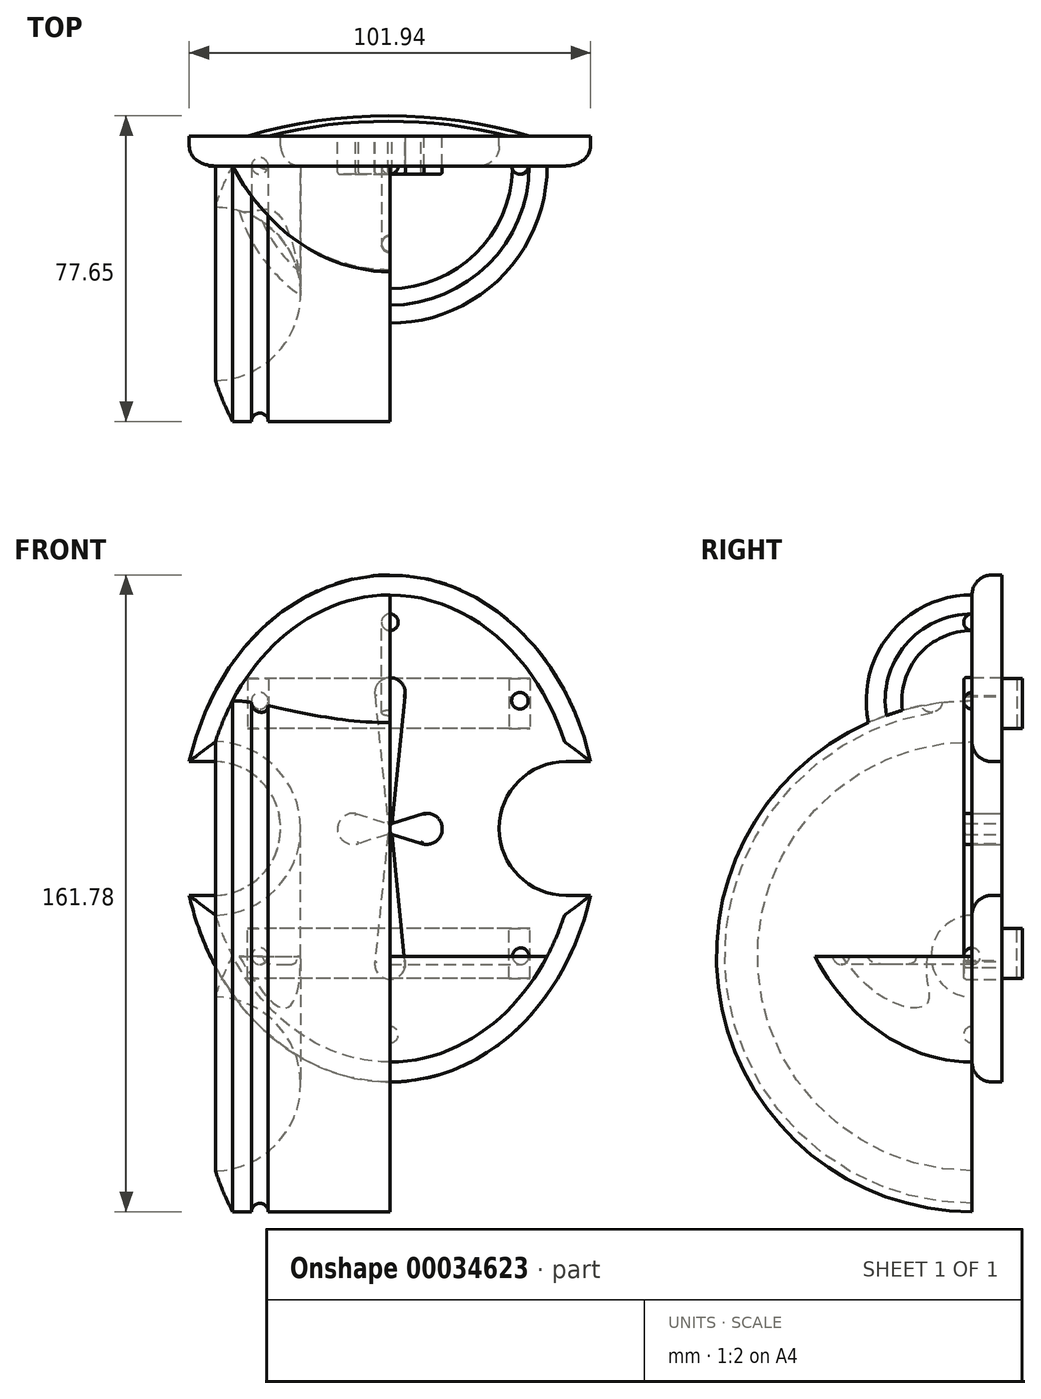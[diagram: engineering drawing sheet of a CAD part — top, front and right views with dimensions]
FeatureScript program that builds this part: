
annotation { "Feature Type Name" : "Feature", "Feature Type Description" : "" }
export const myFeature = defineFeature(function(context is Context, id is Id, definition is map)
    precondition{}
    {
        {
            var Q0;
            Q0=qCreatedBy(makeId("Front.planeOp"),FACE);
            var sketch = newSketch(context, id + "F0", { "sketchPlane" : qUnion([Q0])});
            skEllipticalArc(sketch, "E0", {});
            skLineSegment(sketch, "E1", {"start": v(-52.84, 0) * mm, "end": v(52.84, 0) * mm, "construction": true});
            skLineSegment(sketch, "E2", {"start": v(0, 64.42) * mm, "end": v(0, -64.42) * mm, "construction": true});
            skLineSegment(sketch, "E3.rect.bottom", {"start": v(-50.97, 16.98) * mm, "end": v(-44.74, 16.98) * mm});
            skLineSegment(sketch, "E3.rect.top", {"start": v(-50.97, -16.98) * mm, "end": v(-44.74, -16.98) * mm});
            skPoint(sketch, "E3.rect.middle", {"position": v(-52.84, 0) * mm});
            skArc(sketch, "E4", {"start": v(-44.74, -16.98) * mm, "mid": v(-27.76, 0) * mm, "end": v(-44.74, 16.98) * mm});
            skPoint(sketch, "E5.orphan", {"position": v(-60.94, -16.98) * mm});
            skPoint(sketch, "E6.orphan", {"position": v(-60.94, 16.98) * mm});
            skArc(sketch, "E7.MirrorCS", {"start": v(44.74, -16.98) * mm, "mid": v(27.76, 0) * mm, "end": v(44.74, 16.98) * mm});
            skLineSegment(sketch, "E8.MirrorCS", {"start": v(50.97, 16.98) * mm, "end": v(44.74, 16.98) * mm});
            skLineSegment(sketch, "E9.MirrorCS", {"start": v(50.97, -16.98) * mm, "end": v(44.74, -16.98) * mm});
            skEllipticalArc(sketch, "E10.trimOffspring", {});
            const initialGuessF0  = {"E0": [0, 0, 0, 1, 0.06441504676594614, 0.05284112137579867, 1.837603001446633, 4.4455823057329535], "E10.trimOffspring": [0, 0, 0, 1, 0.06441504676594614, 0.05284112137579867, 4.979195655036426, 1.30398965214316]};
            skSetInitialGuess(sketch, initialGuessF0);
            skSolve(sketch);
        }
        {
            var Q0;
            Q0 = qSketchRegion(id + "F0", true);
            extrude(context, id + "F1", {"entities" : qUnion([Q0]), "depth" : 7.62 * mm});
        }
        {
            var Q0;
            Q0=makeQuery(id+"F1.opExtrude","CAP_EDGE",EDGE,{"disambiguationData":[OSD([sQuery(id+"F0.wireOp",EDGE,"E10.trimOffspring")])],"isStart":false});
            var Q1;
            Q1=makeQuery(id+"F1.opExtrude","CAP_EDGE",EDGE,{"disambiguationData":[OSD([sQuery(id+"F0.wireOp",EDGE,"E7.MirrorCS")])],"isStart":false});
            var Q2;
            Q2=makeQuery(id+"F1.opExtrude","CAP_EDGE",EDGE,{"disambiguationData":[OSD([sQuery(id+"F0.wireOp",EDGE,"E0")])],"isStart":false});
            var Q3;
            Q3=makeQuery(id+"F1.opExtrude","CAP_EDGE",EDGE,{"disambiguationData":[OSD([sQuery(id+"F0.wireOp",EDGE,"E9.MirrorCS")])],"isStart":false});
            var Q4;
            Q4=makeQuery(id+"F1.opExtrude","CAP_EDGE",EDGE,{"disambiguationData":[OSD([sQuery(id+"F0.wireOp",EDGE,"E4")])],"isStart":false});
            var Q5;
            Q5=makeQuery(id+"F1.opExtrude","CAP_EDGE",EDGE,{"disambiguationData":[OSD([sQuery(id+"F0.wireOp",EDGE,"E3.rect.top")])],"isStart":false});
            var Q6;
            Q6=makeQuery(id+"F1.opExtrude","CAP_EDGE",EDGE,{"disambiguationData":[OSD([sQuery(id+"F0.wireOp",EDGE,"E3.rect.bottom")])],"isStart":false});
            var Q7;
            Q7=makeQuery(id+"F1.opExtrude","CAP_EDGE",EDGE,{"disambiguationData":[OSD([sQuery(id+"F0.wireOp",EDGE,"E8.MirrorCS")])],"isStart":false});
            fillet(context, id + "F2", {"entities" : qUnion([Q0, Q1, Q2, Q3, Q4, Q5, Q6, Q7]), "radius" : 5.08 * mm, "tangentPropagation" : true, "allowEdgeOverflow" : false});
        }
        {
            var Q0;
            Q0=qCreatedBy(makeId("Top.planeOp"),FACE);
            cPlane(context, id + "F3", {"entities" : qUnion([Q0]), "cplaneType" : CPlaneType.OFFSET, "offset" : 31.75 * mm, "width" : 152.4 * mm, "height" : 152.4 * mm});
        }
        {
            var Q0;
            Q0=qCreatedBy(id+"F3.planeOp",FACE);
            var sketch = newSketch(context, id + "F4", { "sketchPlane" : qUnion([Q0])});
            skArc(sketch, "E11", {"start": v(35.55, 0) * mm, "mid": v(-0.33, 5.12) * mm, "end": v(-36.21, 0) * mm});
            skArc(sketch, "E12.0", {"start": v(30.21, 0) * mm, "mid": v(-0.33, 3.74) * mm, "end": v(-30.88, 0) * mm});
            skLineSegment(sketch, "E13", {"start": v(-36.21, 0) * mm, "end": v(35.55, 0) * mm});
            skSolve(sketch);
        }
        {
            var Q0;
            {var subQ2=sQuery(id+"F4.wireOp",EDGE,"E11");Q0=makeQuery(id+"F4.imprint","IMPRINT",FACE,{"disambiguationData":[TD([[makeQuery(id+"F4.imprint","IMPRINT",EDGE,{"derivedFrom":subQ2}),1.0]])]});}
            extrude(context, id + "F5", {"entities" : qUnion([Q0]), "endBound" : BoundingType.SYMMETRIC, "depth" : 12.7 * mm});
        }
        {
            var Q0;
            Q0=makeQuery(id+"F5.opExtrude","SWEPT_BODY",BODY,{"disambiguationData":[OSD([sQuery(id+"F4.wireOp",EDGE,"E11"),sQuery(id+"F4.wireOp",EDGE,"E12.0"),sQuery(id+"F4.wireOp",EDGE,"E13")])]});
            var Q1;
            Q1=qCreatedBy(makeId("Top.planeOp"),FACE);
            mirror(context, id + "F6", {"operationType" : NewBodyOperationType.ADD, "entities" : qUnion([Q0]), "mirrorPlane" : qUnion([Q1])});
        }
        {
            var Q0;
            Q0=makeQuery(id+"F1.opExtrude","CAP_FACE",FACE,{"disambiguationData":[OSD([sQuery(id+"F0.wireOp",EDGE,"E0"),sQuery(id+"F0.wireOp",EDGE,"E3.rect.bottom"),sQuery(id+"F0.wireOp",EDGE,"E3.rect.top"),sQuery(id+"F0.wireOp",EDGE,"E4"),sQuery(id+"F0.wireOp",EDGE,"E7.MirrorCS"),sQuery(id+"F0.wireOp",EDGE,"E8.MirrorCS"),sQuery(id+"F0.wireOp",EDGE,"E9.MirrorCS"),sQuery(id+"F0.wireOp",EDGE,"E10.trimOffspring")])],"isStart":false});
            var sketch = newSketch(context, id + "F7", { "sketchPlane" : qUnion([Q0])});
            skArc(sketch, "E14.0", {"start": v(-44.33, 22.06) * mm, "mid": v(-22.68, 0) * mm, "end": v(-44.33, -22.06) * mm});
            skArc(sketch, "E15.1", {"start": v(44.33, -22.06) * mm, "mid": v(22.68, 0) * mm, "end": v(44.33, 22.06) * mm});
            skFitSpline(sketch, "E16.2", {"points": [v(45.82, 17) * mm, v(44.63, 21.22) * mm, v(43.48, 24.58) * mm, v(42.51, 27.05) * mm, v(41.46, 29.46) * mm, v(40.3, 31.83) * mm, v(39.05, 34.15) * mm, v(37.7, 36.41) * mm, v(36.26, 38.62) * mm, v(34.7, 40.77) * mm, v(33.04, 42.84) * mm, v(31.3, 44.81) * mm, v(29.46, 46.7) * mm, v(27.52, 48.5) * mm, v(25.82, 49.9) * mm, v(24.41, 50.98) * mm, v(22.98, 52) * mm, v(21.14, 53.22) * mm, v(18.85, 54.53) * mm, v(16.5, 55.7) * mm, v(14.46, 56.56) * mm, v(12.8, 57.17) * mm, v(11.11, 57.72) * mm, v(9, 58.3) * mm, v(6.42, 58.82) * mm, v(3.81, 59.17) * mm, v(1.18, 59.35) * mm, v(-1.5, 59.34) * mm, v(-4.15, 59.14) * mm, v(-6.77, 58.76) * mm, v(-9.33, 58.22) * mm, v(-11.84, 57.5) * mm, v(-14.31, 56.63) * mm, v(-16.73, 55.59) * mm, v(-19.11, 54.39) * mm, v(-21.4, 53.06) * mm, v(-23.58, 51.6) * mm, v(-25.68, 50.03) * mm, v(-27.7, 48.34) * mm, v(-29.63, 46.53) * mm, v(-31.48, 44.62) * mm, v(-33.2, 42.63) * mm, v(-34.84, 40.58) * mm, v(-36.37, 38.45) * mm, v(-37.8, 36.25) * mm, v(-39.14, 34) * mm, v(-40.39, 31.67) * mm, v(-41.54, 29.28) * mm, v(-42.6, 26.85) * mm, v(-43.87, 23.56) * mm, v(-45.21, 19.34) * mm, v(-46.43, 14.21) * mm, v(-47.13, 9.87) * mm, v(-47.5, 6.36) * mm, v(-47.74, 2.84) * mm, v(-47.8, -1.54) * mm, v(-47.56, -5.9) * mm, v(-47.17, -9.38) * mm, v(-46.79, -11.99) * mm, v(-46.3, -14.58) * mm, v(-45.53, -18.04) * mm, v(-44.33, -22.26) * mm, v(-42.51, -27.19) * mm, v(-40.67, -31.17) * mm, v(-38.98, -34.29) * mm, v(-37.62, -36.55) * mm, v(-36.16, -38.75) * mm, v(-34.1, -41.58) * mm, v(-31.83, -44.27) * mm, v(-29.35, -46.8) * mm, v(-26.75, -49.2) * mm, v(-23.99, -51.35) * mm, v(-21.41, -53.03) * mm, v(-19.9, -53.93) * mm, v(-18.34, -54.79) * mm, v(-16.36, -55.76) * mm, v(-13.93, -56.78) * mm, v(-11.44, -57.63) * mm, v(-9.32, -58.2) * mm, v(-7.6, -58.58) * mm, v(-5.84, -58.9) * mm, v(-3.66, -59.19) * mm, v(-1.04, -59.35) * mm, v(1.58, -59.33) * mm, v(4.2, -59.13) * mm, v(6.38, -58.82) * mm, v(8.12, -58.47) * mm, v(9.84, -58.07) * mm, v(11.95, -57.47) * mm, v(14.42, -56.58) * mm, v(16.83, -55.54) * mm, v(19.19, -54.35) * mm, v(21.48, -53) * mm, v(23.7, -51.52) * mm, v(25.8, -49.93) * mm, v(27.8, -48.24) * mm, v(29.72, -46.44) * mm, v(31.54, -44.55) * mm, v(32.98, -42.9) * mm, v(34.1, -41.52) * mm, v(35.17, -40.12) * mm, v(36.45, -38.33) * mm, v(37.88, -36.13) * mm, v(39.65, -33.13) * mm, v(41.6, -29.26) * mm, v(43.25, -25.24) * mm, v(44.39, -21.93) * mm, v(45.02, -19.82) * mm, v(45.48, -18.12) * mm, v(45.9, -16.41) * mm, v(46.37, -14.27) * mm, v(46.84, -11.7) * mm, v(47.33, -8.25) * mm, v(47.72, -3.9) * mm, v(47.8, 0.46) * mm, v(47.67, 3.98) * mm, v(47.41, 7.5) * mm, v(46.86, 11.84) * mm, v(45.82, 17) * mm, v(44.63, 21.22) * mm, v(43.48, 24.58) * mm]});
            skFitSpline(sketch, "E17.2", {"points": [v(45.82, 17) * mm, v(44.63, 21.22) * mm, v(43.48, 24.58) * mm, v(42.51, 27.05) * mm, v(41.46, 29.46) * mm, v(40.3, 31.83) * mm, v(39.05, 34.15) * mm, v(37.7, 36.41) * mm, v(36.26, 38.62) * mm, v(34.7, 40.77) * mm, v(33.04, 42.84) * mm, v(31.3, 44.81) * mm, v(29.46, 46.7) * mm, v(27.52, 48.5) * mm, v(25.82, 49.9) * mm, v(24.41, 50.98) * mm, v(22.98, 52) * mm, v(21.14, 53.22) * mm, v(18.85, 54.53) * mm, v(16.5, 55.7) * mm, v(14.46, 56.56) * mm, v(12.8, 57.17) * mm, v(11.11, 57.72) * mm, v(9, 58.3) * mm, v(6.42, 58.82) * mm, v(3.81, 59.17) * mm, v(1.18, 59.35) * mm, v(-1.5, 59.34) * mm, v(-4.15, 59.14) * mm, v(-6.77, 58.76) * mm, v(-9.33, 58.22) * mm, v(-11.84, 57.5) * mm, v(-14.31, 56.63) * mm, v(-16.73, 55.59) * mm, v(-19.11, 54.39) * mm, v(-21.4, 53.06) * mm, v(-23.58, 51.6) * mm, v(-25.68, 50.03) * mm, v(-27.7, 48.34) * mm, v(-29.63, 46.53) * mm, v(-31.48, 44.62) * mm, v(-33.2, 42.63) * mm, v(-34.84, 40.58) * mm, v(-36.37, 38.45) * mm, v(-37.8, 36.25) * mm, v(-39.14, 34) * mm, v(-40.39, 31.67) * mm, v(-41.54, 29.28) * mm, v(-42.6, 26.85) * mm, v(-43.87, 23.56) * mm, v(-45.21, 19.34) * mm, v(-46.43, 14.21) * mm, v(-47.13, 9.87) * mm, v(-47.5, 6.36) * mm, v(-47.74, 2.84) * mm, v(-47.8, -1.54) * mm, v(-47.56, -5.9) * mm, v(-47.17, -9.38) * mm, v(-46.79, -11.99) * mm, v(-46.3, -14.58) * mm, v(-45.53, -18.04) * mm, v(-44.33, -22.26) * mm, v(-42.51, -27.19) * mm, v(-40.67, -31.17) * mm, v(-38.98, -34.29) * mm, v(-37.62, -36.55) * mm, v(-36.16, -38.75) * mm, v(-34.1, -41.58) * mm, v(-31.83, -44.27) * mm, v(-29.35, -46.8) * mm, v(-26.75, -49.2) * mm, v(-23.99, -51.35) * mm, v(-21.41, -53.03) * mm, v(-19.9, -53.93) * mm, v(-18.34, -54.79) * mm, v(-16.36, -55.76) * mm, v(-13.93, -56.78) * mm, v(-11.44, -57.63) * mm, v(-9.32, -58.2) * mm, v(-7.6, -58.58) * mm, v(-5.84, -58.9) * mm, v(-3.66, -59.19) * mm, v(-1.04, -59.35) * mm, v(1.58, -59.33) * mm, v(4.2, -59.13) * mm, v(6.38, -58.82) * mm, v(8.12, -58.47) * mm, v(9.84, -58.07) * mm, v(11.95, -57.47) * mm, v(14.42, -56.58) * mm, v(16.83, -55.54) * mm, v(19.19, -54.35) * mm, v(21.48, -53) * mm, v(23.7, -51.52) * mm, v(25.8, -49.93) * mm, v(27.8, -48.24) * mm, v(29.72, -46.44) * mm, v(31.54, -44.55) * mm, v(32.98, -42.9) * mm, v(34.1, -41.52) * mm, v(35.17, -40.12) * mm, v(36.45, -38.33) * mm, v(37.88, -36.13) * mm, v(39.65, -33.13) * mm, v(41.6, -29.26) * mm, v(43.25, -25.24) * mm, v(44.39, -21.93) * mm, v(45.02, -19.82) * mm, v(45.48, -18.12) * mm, v(45.9, -16.41) * mm, v(46.37, -14.27) * mm, v(46.84, -11.7) * mm, v(47.33, -8.25) * mm, v(47.72, -3.9) * mm, v(47.8, 0.46) * mm, v(47.67, 3.98) * mm, v(47.41, 7.5) * mm, v(46.86, 11.84) * mm, v(45.82, 17) * mm, v(44.63, 21.22) * mm, v(43.48, 24.58) * mm]});
            skFitSpline(sketch, "E17.3", {"points": [v(-45.82, -17) * mm, v(-44.63, -21.23) * mm, v(-43.47, -24.58) * mm, v(-42.51, -27.05) * mm, v(-41.45, -29.47) * mm, v(-40.3, -31.84) * mm, v(-39.05, -34.15) * mm, v(-37.7, -36.41) * mm, v(-36.25, -38.62) * mm, v(-34.7, -40.77) * mm, v(-33.04, -42.84) * mm, v(-31.3, -44.82) * mm, v(-29.45, -46.7) * mm, v(-27.52, -48.5) * mm, v(-25.82, -49.9) * mm, v(-24.4, -50.98) * mm, v(-22.97, -52.01) * mm, v(-21.13, -53.22) * mm, v(-18.85, -54.53) * mm, v(-16.5, -55.7) * mm, v(-14.46, -56.56) * mm, v(-12.79, -57.17) * mm, v(-11.1, -57.72) * mm, v(-8.99, -58.3) * mm, v(-6.41, -58.83) * mm, v(-3.8, -59.18) * mm, v(-1.17, -59.35) * mm, v(1.5, -59.34) * mm, v(4.16, -59.14) * mm, v(6.77, -58.76) * mm, v(9.33, -58.22) * mm, v(11.85, -57.5) * mm, v(14.32, -56.63) * mm, v(16.74, -55.59) * mm, v(19.12, -54.39) * mm, v(21.4, -53.05) * mm, v(23.59, -51.6) * mm, v(25.68, -50.02) * mm, v(27.7, -48.33) * mm, v(29.63, -46.53) * mm, v(31.48, -44.62) * mm, v(33.21, -42.63) * mm, v(34.84, -40.57) * mm, v(36.37, -38.45) * mm, v(37.8, -36.25) * mm, v(39.14, -34) * mm, v(40.39, -31.67) * mm, v(41.54, -29.28) * mm, v(42.6, -26.85) * mm, v(43.87, -23.55) * mm, v(45.21, -19.34) * mm, v(46.43, -14.2) * mm, v(47.13, -9.87) * mm, v(47.5, -6.35) * mm, v(47.74, -2.83) * mm, v(47.8, 1.55) * mm, v(47.56, 5.9) * mm, v(47.17, 9.39) * mm, v(46.79, 11.99) * mm, v(46.3, 14.59) * mm, v(45.53, 18.04) * mm, v(44.33, 22.26) * mm, v(42.5, 27.2) * mm, v(40.66, 31.17) * mm, v(38.98, 34.29) * mm, v(37.61, 36.56) * mm, v(36.16, 38.75) * mm, v(34.1, 41.59) * mm, v(31.83, 44.27) * mm, v(29.35, 46.8) * mm, v(26.75, 49.2) * mm, v(23.99, 51.35) * mm, v(21.4, 53.04) * mm, v(19.89, 53.93) * mm, v(18.33, 54.79) * mm, v(16.35, 55.76) * mm, v(13.92, 56.78) * mm, v(11.43, 57.63) * mm, v(9.31, 58.2) * mm, v(7.59, 58.59) * mm, v(5.84, 58.9) * mm, v(3.66, 59.2) * mm, v(1.04, 59.35) * mm, v(-1.58, 59.33) * mm, v(-4.2, 59.13) * mm, v(-6.38, 58.82) * mm, v(-8.13, 58.47) * mm, v(-9.85, 58.07) * mm, v(-11.96, 57.47) * mm, v(-14.43, 56.58) * mm, v(-16.84, 55.54) * mm, v(-19.19, 54.35) * mm, v(-21.49, 53) * mm, v(-23.7, 51.52) * mm, v(-25.8, 49.93) * mm, v(-27.81, 48.23) * mm, v(-29.72, 46.44) * mm, v(-31.54, 44.55) * mm, v(-32.99, 42.89) * mm, v(-34.1, 41.52) * mm, v(-35.18, 40.11) * mm, v(-36.45, 38.33) * mm, v(-37.88, 36.13) * mm, v(-39.65, 33.13) * mm, v(-41.6, 29.26) * mm, v(-43.25, 25.24) * mm, v(-44.39, 21.93) * mm, v(-45.02, 19.82) * mm, v(-45.48, 18.12) * mm, v(-45.9, 16.4) * mm, v(-46.37, 14.27) * mm, v(-46.84, 11.7) * mm, v(-47.33, 8.24) * mm, v(-47.72, 3.9) * mm, v(-47.8, -0.46) * mm, v(-47.67, -3.98) * mm, v(-47.41, -7.5) * mm, v(-46.86, -11.85) * mm, v(-45.82, -17) * mm, v(-44.63, -21.23) * mm, v(-43.47, -24.58) * mm]});
            skLineSegment(sketch, "E18", {"start": v(-39.96, 32.45) * mm, "end": v(39.96, 32.45) * mm});
            skLineSegment(sketch, "E19.MirrorCS", {"start": v(-39.96, -32.45) * mm, "end": v(40.19, -32.45) * mm});
            skCircle(sketch, "E20", {"center": v(-33.04, 32.45) * mm, "radius": 2.11 * mm});
            skCircle(sketch, "E21", {"center": v(33.03, 32.45) * mm, "radius": 2.11 * mm});
            skCircle(sketch, "E22", {"center": v(-33.03, -32.45) * mm, "radius": 2.11 * mm});
            skCircle(sketch, "E23", {"center": v(33.25, -32.45) * mm, "radius": 2.11 * mm});
            skLineSegment(sketch, "E24", {"start": v(0, 59.34) * mm, "end": v(0, -59.34) * mm});
            skCircle(sketch, "E25", {"center": v(0, 52.4) * mm, "radius": 2.11 * mm});
            skCircle(sketch, "E26", {"center": v(0, -52.4) * mm, "radius": 2.11 * mm});
            skSolve(sketch);
        }
        {
            var Q0;
            {var subQ0=sQuery(id+"F7.wireOp",EDGE,"E20");var subQ1=sQuery(id+"F7.wireOp",EDGE,"E18");var subQ3=makeQuery(id+"F7.imprint","INTERSECT",VERTEX,{"disambiguationData":[OD(0.0)],"derivedFrom":[subQ1,subQ0]});Q0=makeQuery(id+"F7.imprint","IMPRINT",FACE,{"disambiguationData":[TD([[makeQuery(id+"F7.imprint","IMPRINT",EDGE,{"disambiguationData":[TD([[subQ3,-1.0]])],"derivedFrom":subQ1}),1.0]])]});}
            var Q1;
            Q1=sQuery(id+"F7.wireOp",EDGE,"E18");
            revolve(context, id + "F8", {"operationType" : NewBodyOperationType.ADD, "entities" : qUnion([Q0]), "axis" : qUnion([Q1]), "revolveType" : RevolveType.ONE_DIRECTION, "angle" : 180 * degree});
        }
        {
            var Q0;
            {var subQ0=sQuery(id+"F7.wireOp",EDGE,"E25");var subQ1=sQuery(id+"F7.wireOp",EDGE,"E24");var subQ3=makeQuery(id+"F7.imprint","INTERSECT",VERTEX,{"disambiguationData":[OD(0.0)],"derivedFrom":[subQ1,subQ0]});Q0=makeQuery(id+"F7.imprint","IMPRINT",FACE,{"disambiguationData":[TD([[makeQuery(id+"F7.imprint","IMPRINT",EDGE,{"disambiguationData":[TD([[subQ3,1.0]])],"derivedFrom":subQ1}),1.0]])]});}
            var Q1;
            Q1=sQuery(id+"F7.wireOp",EDGE,"E24");
            revolve(context, id + "F9", {"operationType" : NewBodyOperationType.ADD, "entities" : qUnion([Q0]), "axis" : qUnion([Q1]), "revolveType" : RevolveType.ONE_DIRECTION, "angle" : 180 * degree});
        }
        {
            var Q0;
            {var subQ0=sQuery(id+"F7.wireOp",EDGE,"E21");var subQ1=sQuery(id+"F7.wireOp",EDGE,"E18");var subQ3=makeQuery(id+"F7.imprint","INTERSECT",VERTEX,{"disambiguationData":[OD(0.0)],"derivedFrom":[subQ1,subQ0]});Q0=makeQuery(id+"F7.imprint","IMPRINT",FACE,{"disambiguationData":[TD([[makeQuery(id+"F7.imprint","IMPRINT",EDGE,{"disambiguationData":[TD([[subQ3,-1.0]])],"derivedFrom":subQ1}),-1.0]])]});}
            var Q1;
            Q1=sQuery(id+"F7.wireOp",EDGE,"E18");
            revolve(context, id + "F10", {"operationType" : NewBodyOperationType.ADD, "entities" : qUnion([Q0]), "axis" : qUnion([Q1]), "revolveType" : RevolveType.ONE_DIRECTION, "oppositeDirection" : true, "angle" : 180 * degree});
        }
        {
            var Q0;
            {var subQ0=sQuery(id+"F7.wireOp",EDGE,"E22");var subQ1=sQuery(id+"F7.wireOp",EDGE,"E19.MirrorCS");var subQ3=makeQuery(id+"F7.imprint","INTERSECT",VERTEX,{"disambiguationData":[OD(0.0)],"derivedFrom":[subQ1,subQ0]});Q0=makeQuery(id+"F7.imprint","IMPRINT",FACE,{"disambiguationData":[TD([[makeQuery(id+"F7.imprint","IMPRINT",EDGE,{"disambiguationData":[TD([[subQ3,-1.0]])],"derivedFrom":subQ1}),1.0]])]});}
            var Q1;
            Q1=sQuery(id+"F7.wireOp",EDGE,"E19.MirrorCS");
            revolve(context, id + "F11", {"operationType" : NewBodyOperationType.ADD, "entities" : qUnion([Q0]), "axis" : qUnion([Q1]), "revolveType" : RevolveType.ONE_DIRECTION, "angle" : 180 * degree});
        }
        {
            var Q0;
            {var subQ0=sQuery(id+"F7.wireOp",EDGE,"E23");var subQ1=sQuery(id+"F7.wireOp",EDGE,"E19.MirrorCS");var subQ3=makeQuery(id+"F7.imprint","INTERSECT",VERTEX,{"disambiguationData":[OD(0.0)],"derivedFrom":[subQ1,subQ0]});Q0=makeQuery(id+"F7.imprint","IMPRINT",FACE,{"disambiguationData":[TD([[makeQuery(id+"F7.imprint","IMPRINT",EDGE,{"disambiguationData":[TD([[subQ3,-1.0]])],"derivedFrom":subQ1}),-1.0]])]});}
            var Q1;
            Q1=sQuery(id+"F7.wireOp",EDGE,"E19.MirrorCS");
            revolve(context, id + "F12", {"operationType" : NewBodyOperationType.ADD, "entities" : qUnion([Q0]), "axis" : qUnion([Q1]), "revolveType" : RevolveType.ONE_DIRECTION, "oppositeDirection" : true, "angle" : 180 * degree});
        }
        {
            var Q0;
            {var subQ0=sQuery(id+"F7.wireOp",EDGE,"E26");var subQ1=sQuery(id+"F7.wireOp",EDGE,"E24");var subQ3=makeQuery(id+"F7.imprint","INTERSECT",VERTEX,{"disambiguationData":[OD(0.0)],"derivedFrom":[subQ1,subQ0]});Q0=makeQuery(id+"F7.imprint","IMPRINT",FACE,{"disambiguationData":[TD([[makeQuery(id+"F7.imprint","IMPRINT",EDGE,{"disambiguationData":[TD([[subQ3,1.0]])],"derivedFrom":subQ1}),1.0]])]});}
            var Q1;
            Q1=sQuery(id+"F7.wireOp",EDGE,"E24");
            revolve(context, id + "F13", {"operationType" : NewBodyOperationType.ADD, "entities" : qUnion([Q0]), "axis" : qUnion([Q1]), "revolveType" : RevolveType.ONE_DIRECTION, "angle" : 180 * degree});
        }
        {
            var Q0;
            Q0=qCreatedBy(makeId("Front.planeOp"),FACE);
            var sketch = newSketch(context, id + "F14", { "sketchPlane" : qUnion([Q0])});
            skLineSegment(sketch, "E27.rect.bottom", {"start": v(-1.24, 38.1) * mm, "end": v(3.81, 38.1) * mm});
            skLineSegment(sketch, "E27.rect.top", {"start": v(-1.24, -38.1) * mm, "end": v(1.29, -38.1) * mm});
            skLineSegment(sketch, "E27.rect.left", {"start": v(-3.8, 35.04) * mm, "end": v(-3.8, 33.82) * mm});
            skLineSegment(sketch, "E27.rect.right", {"start": v(3.81, 35.28) * mm, "end": v(3.81, 33.58) * mm});
            skPoint(sketch, "E27.rect.middle", {"position": v(0, 0) * mm});
            skLineSegment(sketch, "E28.rect.bottom", {"start": v(-9.98, 3.81) * mm, "end": v(-8.7, 3.81) * mm});
            skLineSegment(sketch, "E28.rect.top", {"start": v(-10.73, -3.81) * mm, "end": v(-7.95, -3.81) * mm});
            skLineSegment(sketch, "E28.rect.left", {"start": v(-13.22, 0.7) * mm, "end": v(-13.22, -0.9) * mm});
            skLineSegment(sketch, "E28.rect.right", {"start": v(13.22, 0.7) * mm, "end": v(13.22, -0.9) * mm});
            skPoint(sketch, "E29.visualSharp", {"position": v(-3.8, 38.1) * mm});
            skArc(sketch, "E29.filletArc", {"start": v(-3.5, 38.1) * mm, "mid": v(-3.72, 38) * mm, "end": v(-3.8, 37.78) * mm});
            skArc(sketch, "E30", {"start": v(3.81, 33.58) * mm, "mid": v(0.14, 38.3) * mm, "end": v(-3.8, 33.82) * mm});
            skArc(sketch, "E31.MirrorCS", {"start": v(3.8, -33.58) * mm, "mid": v(0.14, -38.3) * mm, "end": v(-3.81, -33.82) * mm});
            skArc(sketch, "E32", {"start": v(-8.7, 3.81) * mm, "mid": v(-13.28, -0.49) * mm, "end": v(-7.95, -3.81) * mm});
            skArc(sketch, "E33.MirrorCS", {"start": v(8.7, 3.81) * mm, "mid": v(13.28, -0.49) * mm, "end": v(7.95, -3.81) * mm});
            skPoint(sketch, "E34.orphan", {"position": v(-13.22, 3.81) * mm});
            skPoint(sketch, "E35.orphan", {"position": v(-13.22, -3.81) * mm});
            skPoint(sketch, "E36.orphan", {"position": v(3.8, -38.1) * mm});
            skPoint(sketch, "E37.orphan", {"position": v(-3.81, -38.1) * mm});
            skPoint(sketch, "E38.orphan", {"position": v(13.22, -3.81) * mm});
            skPoint(sketch, "E39.orphan", {"position": v(13.22, 3.81) * mm});
            skLineSegment(sketch, "E40", {"start": v(-8.7, 3.81) * mm, "end": v(-0.51, 1.25) * mm});
            skLineSegment(sketch, "E41", {"start": v(-3.8, 33.82) * mm, "end": v(-0.51, 1.25) * mm});
            skLineSegment(sketch, "E42", {"start": v(0.53, -1.46) * mm, "end": v(3.8, -35.28) * mm});
            skLineSegment(sketch, "E43.trimOffspring", {"start": v(-0.77, 3.81) * mm, "end": v(0.78, 3.81) * mm});
            skLineSegment(sketch, "E44.trimOffspring", {"start": v(8.7, 3.81) * mm, "end": v(9.98, 3.81) * mm});
            skLineSegment(sketch, "E45.trimOffspring", {"start": v(-3.81, -33.82) * mm, "end": v(-3.81, -35.04) * mm});
            skLineSegment(sketch, "E46.trimOffspring", {"start": v(3.8, -33.58) * mm, "end": v(3.8, -35.28) * mm});
            skLineSegment(sketch, "E47.trimOffspring", {"start": v(3.8, -3.81) * mm, "end": v(10.73, -3.81) * mm});
            skLineSegment(sketch, "E48.trimOffspring", {"start": v(-0.75, -3.81) * mm, "end": v(0.76, -3.81) * mm});
            skPoint(sketch, "E49.orphan", {"position": v(0.02, 3.81) * mm});
            skPoint(sketch, "E50.orphan", {"position": v(-3.8, 0.7) * mm});
            skLineSegment(sketch, "E51.trimOffspring", {"start": v(0.52, 1.32) * mm, "end": v(3.81, 33.58) * mm});
            skPoint(sketch, "E52.orphan", {"position": v(3.81, -0.1) * mm});
            skPoint(sketch, "E53.trimOffspring.end.orphan", {"position": v(0, -3.81) * mm});
            skLineSegment(sketch, "E54.trimOffspring", {"start": v(-0.51, -1.46) * mm, "end": v(-7.95, -3.8) * mm});
            skLineSegment(sketch, "E55.trimOffspring", {"start": v(-0.51, -1.46) * mm, "end": v(-3.81, -33.82) * mm});
            skPoint(sketch, "E56.orphan", {"position": v(0.3, 1.25) * mm});
            skPoint(sketch, "E57.trimOffspring.start.orphan", {"position": v(0.3, 1) * mm});
            skLineSegment(sketch, "E58", {"start": v(8.7, 3.81) * mm, "end": v(0.52, 1.32) * mm});
            skLineSegment(sketch, "E59", {"start": v(0.53, -1.46) * mm, "end": v(7.95, -3.8) * mm});
            skPoint(sketch, "E60.endSnap0", {"position": v(0.02, -38.1) * mm});
            skSolve(sketch);
        }
        {
            var Q0;
            Q0 = qSketchRegion(id + "F14", true);
            extrude(context, id + "F15", {"entities" : qUnion([Q0]), "depth" : 9.65 * mm});
        }
        {
            var Q0;
            Q0=makeQuery(id+"F15.opExtrude","CAP_EDGE",EDGE,{"disambiguationData":[OSD([sQuery(id+"F14.wireOp",EDGE,"E51.trimOffspring")])],"isStart":false});
            var Q1;
            Q1=makeQuery(id+"F15.opExtrude","CAP_EDGE",EDGE,{"disambiguationData":[OSD([sQuery(id+"F14.wireOp",EDGE,"E41")])],"isStart":false});
            var Q2;
            Q2=makeQuery(id+"F15.opExtrude","CAP_EDGE",EDGE,{"disambiguationData":[OSD([sQuery(id+"F14.wireOp",EDGE,"E30")])],"isStart":false});
            var Q3;
            Q3=makeQuery(id+"F15.opExtrude","CAP_EDGE",EDGE,{"disambiguationData":[OSD([sQuery(id+"F14.wireOp",EDGE,"E58")])],"isStart":false});
            var Q4;
            Q4=makeQuery(id+"F15.opExtrude","CAP_EDGE",EDGE,{"disambiguationData":[OSD([sQuery(id+"F14.wireOp",EDGE,"E59")])],"isStart":false});
            var Q5;
            Q5=makeQuery(id+"F15.opExtrude","CAP_EDGE",EDGE,{"disambiguationData":[OSD([sQuery(id+"F14.wireOp",EDGE,"E33.MirrorCS")])],"isStart":false});
            var Q6;
            Q6=makeQuery(id+"F15.opExtrude","CAP_EDGE",EDGE,{"disambiguationData":[OSD([sQuery(id+"F14.wireOp",EDGE,"E42")])],"isStart":false});
            var Q7;
            {var subQ0=sQuery(id+"F14.wireOp",EDGE,"E31.MirrorCS");var subQ1=sQuery(id+"F14.wireOp",EDGE,"E27.rect.top");var subQ2=makeQuery(id+"F14.imprint","INTERSECT",VERTEX,{"disambiguationData":[OD(1.0)],"derivedFrom":[subQ1,subQ0]});var subQ3=makeQuery(id+"F14.imprint","INTERSECT",VERTEX,{"disambiguationData":[OD(0.0)],"derivedFrom":[subQ1,subQ0]});var subQ4=sQuery(id+"F14.wireOp",EDGE,"E45.trimOffspring");var subQ5=makeQuery(id+"F14.imprint","INTERSECT",VERTEX,{"derivedFrom":[subQ0,subQ4]});Q7=makeQuery(id+"F15.opExtrude","CAP_EDGE",EDGE,{"disambiguationData":[OSD([subQ0]),TDD([makeQuery(id+"F14.imprint","IMPRINT",EDGE,{"disambiguationData":[TD([[subQ2,1.0]])],"derivedFrom":subQ0}),makeQuery(id+"F14.imprint","IMPRINT",EDGE,{"disambiguationData":[TD([[subQ3,1.0]])],"derivedFrom":subQ0}),makeQuery(id+"F14.imprint","IMPRINT",EDGE,{"disambiguationData":[TD([[subQ3,-1.0]])],"derivedFrom":subQ0}),makeQuery(id+"F14.imprint","IMPRINT",EDGE,{"disambiguationData":[TD([[subQ5,-1.0]])],"derivedFrom":subQ0})])],"isStart":false});}
            var Q8;
            Q8=makeQuery(id+"F15.opExtrude","CAP_EDGE",EDGE,{"disambiguationData":[OSD([sQuery(id+"F14.wireOp",EDGE,"E55.trimOffspring")])],"isStart":false});
            var Q9;
            Q9=makeQuery(id+"F15.opExtrude","CAP_EDGE",EDGE,{"disambiguationData":[OSD([sQuery(id+"F14.wireOp",EDGE,"E54.trimOffspring")])],"isStart":false});
            var Q10;
            Q10=makeQuery(id+"F15.opExtrude","CAP_EDGE",EDGE,{"disambiguationData":[OSD([sQuery(id+"F14.wireOp",EDGE,"E32")])],"isStart":false});
            var Q11;
            Q11=makeQuery(id+"F15.opExtrude","CAP_EDGE",EDGE,{"disambiguationData":[OSD([sQuery(id+"F14.wireOp",EDGE,"E40")])],"isStart":false});
            fillet(context, id + "F16", {"entities" : qUnion([Q0, Q1, Q2, Q3, Q4, Q5, Q6, Q7, Q8, Q9, Q10, Q11]), "radius" : 0.5 * mm, "tangentPropagation" : true, "allowEdgeOverflow" : false});
        }
    });
